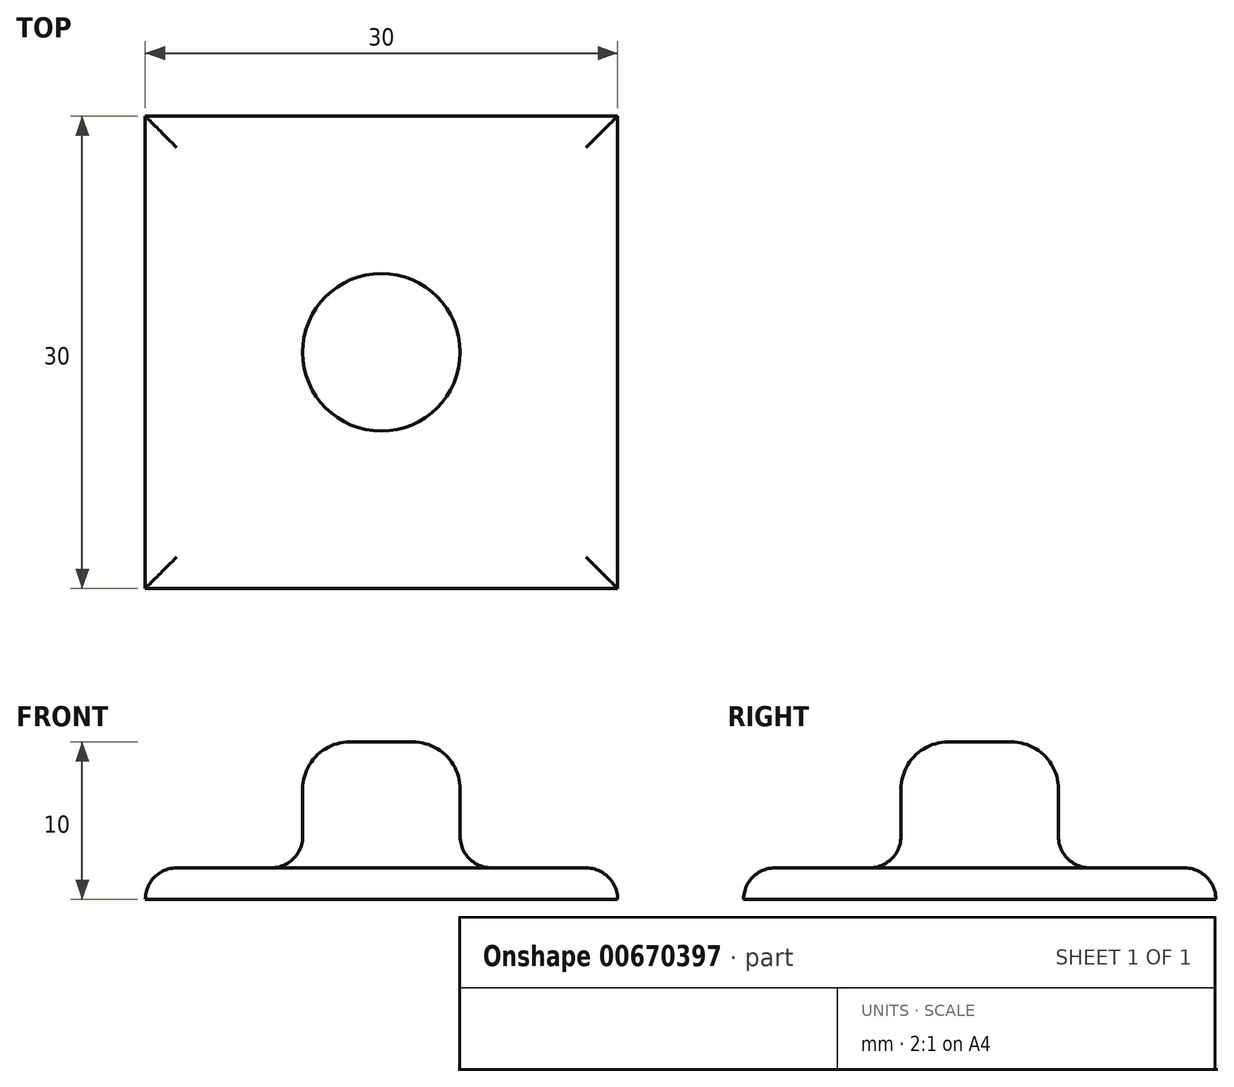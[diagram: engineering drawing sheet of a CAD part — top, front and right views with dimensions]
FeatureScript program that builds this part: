
annotation { "Feature Type Name" : "Feature", "Feature Type Description" : "" }
export const myFeature = defineFeature(function(context is Context, id is Id, definition is map)
    precondition{}
    {
        {
            var Q0;
            Q0=qCreatedBy(makeId("Top.planeOp"),FACE);
            var sketch = newSketch(context, id + "F0", { "sketchPlane" : qUnion([Q0])});
            skLineSegment(sketch, "E0.bottom", {"start": v(15, -15) * mm, "end": v(-15, -15) * mm});
            skLineSegment(sketch, "E0.top", {"start": v(15, 15) * mm, "end": v(-15, 15) * mm});
            skLineSegment(sketch, "E0.left", {"start": v(15, -15) * mm, "end": v(15, 15) * mm});
            skLineSegment(sketch, "E0.right", {"start": v(-15, -15) * mm, "end": v(-15, 15) * mm});
            skPoint(sketch, "E0.middle", {"position": v(0, 0) * mm});
            skSolve(sketch);
        }
        {
            var Q0;
            Q0 = qSketchRegion(id + "F0", true);
            extrude(context, id + "F1", {"entities" : qUnion([Q0]), "depth" : 2 * mm, "offsetDistance" : 25 * mm});
        }
        {
            var Q0;
            Q0=makeQuery(id+"F1.opExtrude","CAP_FACE",FACE,{"disambiguationData":[OSD([sQuery(id+"F0.wireOp",EDGE,"E0.bottom"),sQuery(id+"F0.wireOp",EDGE,"E0.top"),sQuery(id+"F0.wireOp",EDGE,"E0.left"),sQuery(id+"F0.wireOp",EDGE,"E0.right")])],"isStart":false});
            var sketch = newSketch(context, id + "F2", { "sketchPlane" : qUnion([Q0])});
            skCircle(sketch, "E1", {"center": v(0, 0) * mm, "radius": 5 * mm});
            skSolve(sketch);
        }
        {
            var Q0;
            Q0 = qSketchRegion(id + "F2", true);
            extrude(context, id + "F3", {"entities" : qUnion([Q0]), "operationType" : NewBodyOperationType.ADD, "depth" : 8 * mm, "offsetDistance" : 25 * mm});
        }
        {
            var Q0;
            Q0=makeQuery(id+"F3.opExtrude","CAP_EDGE",EDGE,{"disambiguationData":[OSD([sQuery(id+"F2.wireOp",EDGE,"E1")])],"isStart":false});
            fillet(context, id + "F4", {"entities" : qUnion([Q0]), "radius" : 3 * mm, "tangentPropagation" : true, "allowEdgeOverflow" : false});
        }
        {
            var Q0;
            Q0=makeQuery(id+"F1.opExtrude","CAP_FACE",FACE,{"disambiguationData":[OSD([sQuery(id+"F0.wireOp",EDGE,"E0.bottom"),sQuery(id+"F0.wireOp",EDGE,"E0.top"),sQuery(id+"F0.wireOp",EDGE,"E0.left"),sQuery(id+"F0.wireOp",EDGE,"E0.right")])],"isStart":false});
            fillet(context, id + "F5", {"entities" : qUnion([Q0]), "radius" : 2 * mm, "tangentPropagation" : true, "allowEdgeOverflow" : false});
        }
    });
